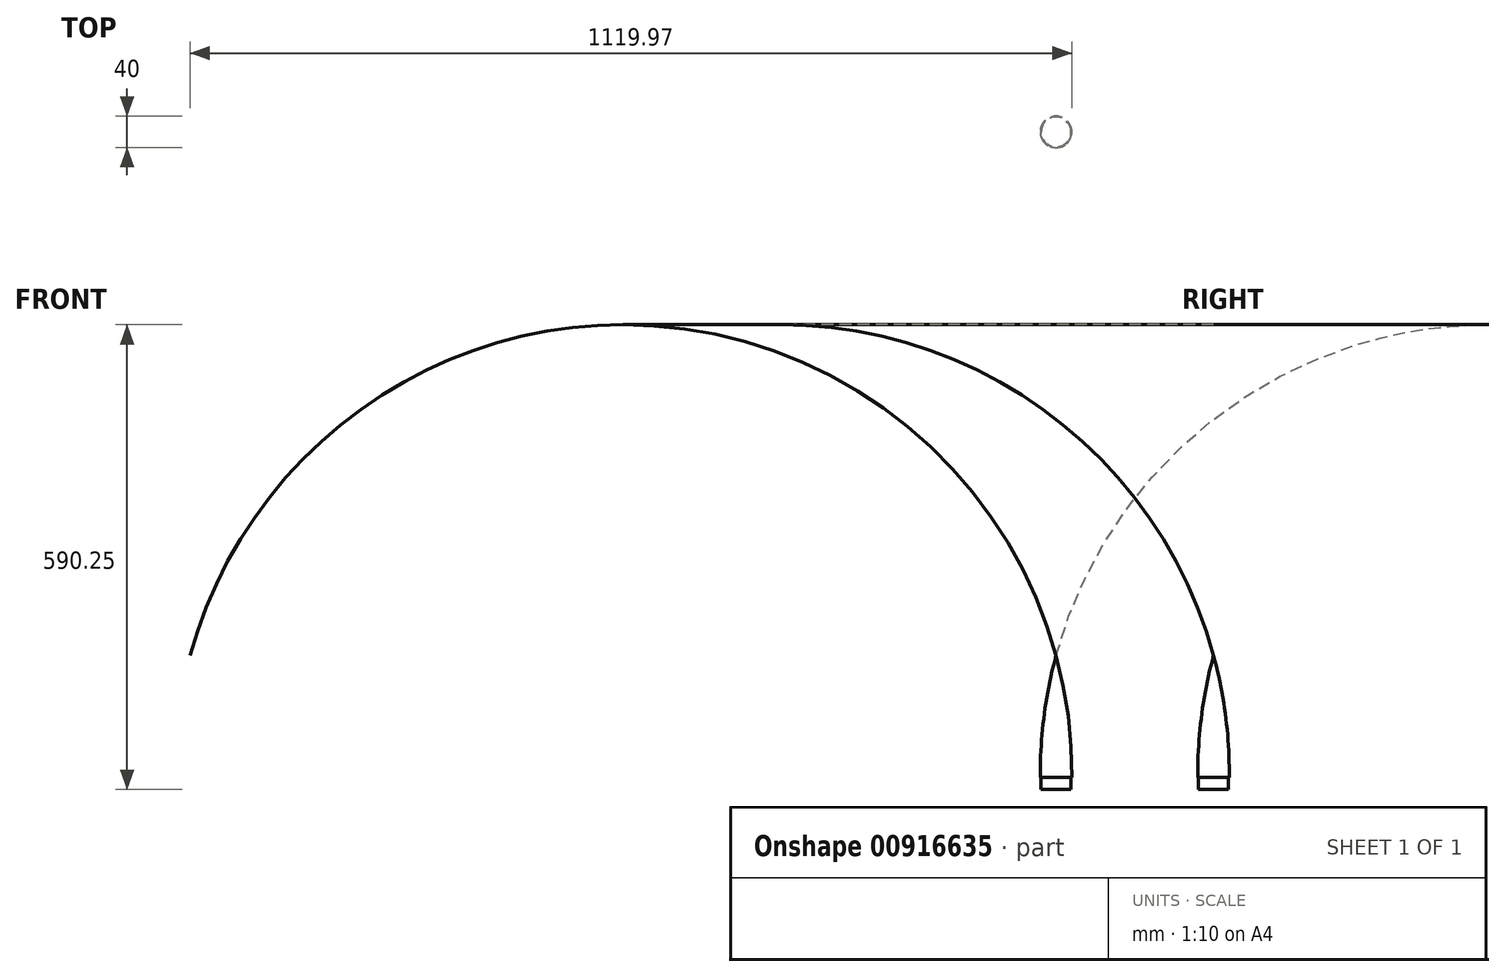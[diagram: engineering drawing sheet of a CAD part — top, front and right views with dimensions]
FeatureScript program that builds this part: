
annotation { "Feature Type Name" : "Feature", "Feature Type Description" : "" }
export const myFeature = defineFeature(function(context is Context, id is Id, definition is map)
    precondition{}
    {
        {
            var Q0;
            Q0=qCreatedBy(makeId("Front.planeOp"),FACE);
            var sketch = newSketch(context, id + "F0", { "sketchPlane" : qUnion([Q0])});
            skLineSegment(sketch, "E0", {"start": v(0, 0) * mm, "end": v(19, 0) * mm});
            skLineSegment(sketch, "E1", {"start": v(19, 0) * mm, "end": v(19, 15) * mm});
            skLineSegment(sketch, "E2", {"start": v(19, 15) * mm, "end": v(20, 15) * mm});
            skLineSegment(sketch, "E3", {"start": v(0, 0) * mm, "end": v(0, 170) * mm, "construction": true});
            skArc(sketch, "E4", {"start": v(20, 15) * mm, "mid": v(15.34, 93.19) * mm, "end": v(0, 170) * mm});
            skLineSegment(sketch, "E5", {"start": v(0, 0) * mm, "end": v(0, 170) * mm});
            skSolve(sketch);
        }
        {
            var Q0;
            Q0=makeQuery(id+"F0.imprint","IMPRINT",FACE,{"disambiguationData":[TD([[makeQuery(id+"F0.imprint","IMPRINT",EDGE,{"derivedFrom":sQuery(id+"F0.wireOp",EDGE,"E0")}),1.0]])]});
            var Q1;
            Q1=sQuery(id+"F0.wireOp",EDGE,"E5");
            revolve(context, id + "F1", {"surfaceOperationType" : NewSurfaceOperationType.NEW, "entities" : qUnion([Q0]), "axis" : qUnion([Q1]), "revolveType" : RevolveType.FULL});
        }
    });
